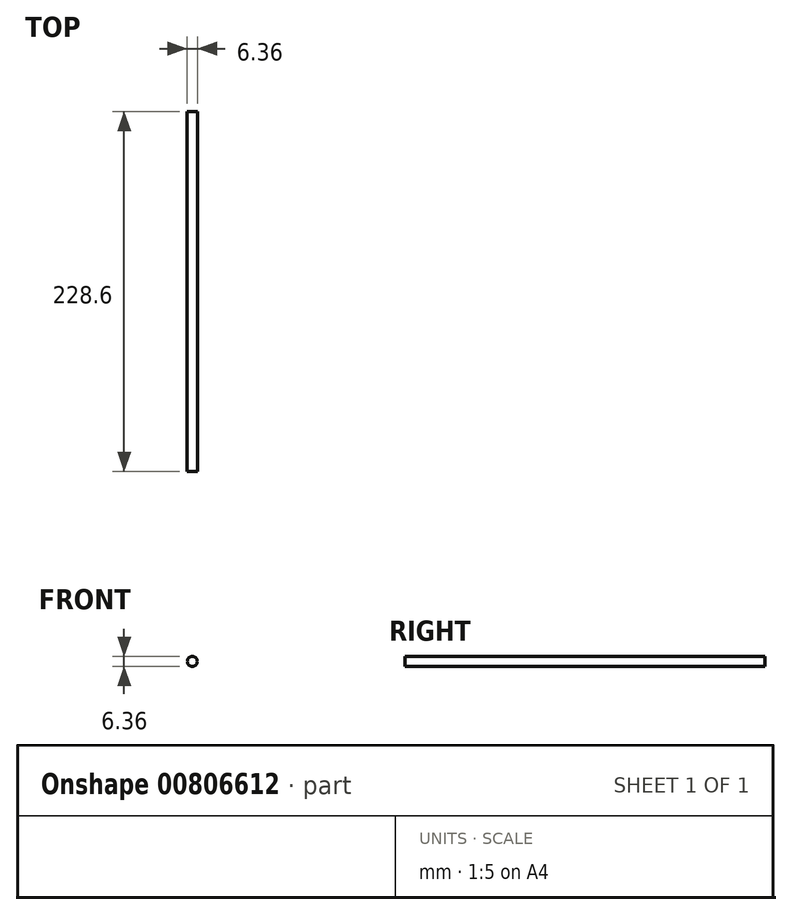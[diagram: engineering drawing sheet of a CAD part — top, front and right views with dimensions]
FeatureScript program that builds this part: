
annotation { "Feature Type Name" : "Feature", "Feature Type Description" : "" }
export const myFeature = defineFeature(function(context is Context, id is Id, definition is map)
    precondition{}
    {
        {
            var Q0;
            Q0=qCreatedBy(makeId("Front.planeOp"),FACE);
            var sketch = newSketch(context, id + "F0", { "sketchPlane" : qUnion([Q0])});
            skCircle(sketch, "E0", {"center": v(0, 0) * mm, "radius": 3.18 * mm});
            skSolve(sketch);
        }
        {
            var Q0;
            Q0 = qSketchRegion(id + "F0", true);
            extrude(context, id + "F1", {"entities" : qUnion([Q0]), "depth" : 228.6 * mm, "offsetDistance" : 25.4 * mm});
        }
    });
